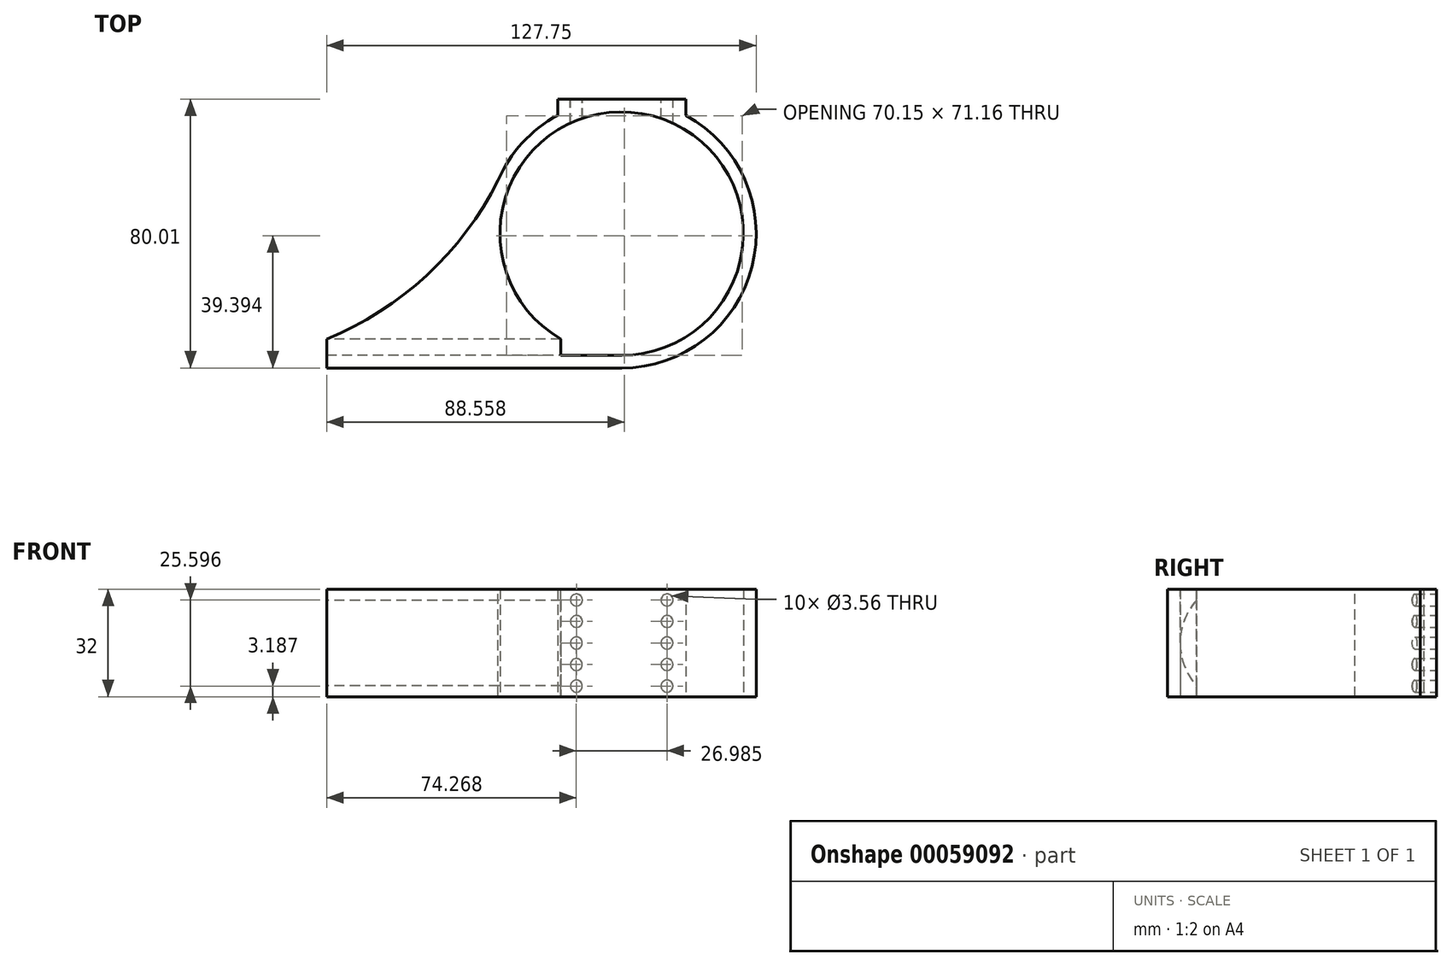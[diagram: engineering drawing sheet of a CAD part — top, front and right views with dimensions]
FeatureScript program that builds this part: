
annotation { "Feature Type Name" : "Feature", "Feature Type Description" : "" }
export const myFeature = defineFeature(function(context is Context, id is Id, definition is map)
    precondition{}
    {
        {
            var Q0;
            Q0=qCreatedBy(makeId("Top.planeOp"),FACE);
            var sketch = newSketch(context, id + "F0", { "sketchPlane" : qUnion([Q0])});
            skPoint(sketch, "E0.visualSharp", {"position": v(52.17, 65.91) * mm});
            skPoint(sketch, "E1.visualSharp", {"position": v(52.17, -14.1) * mm});
            skPoint(sketch, "E2.visualSharp", {"position": v(-27.84, 65.91) * mm});
            skLineSegment(sketch, "E3", {"start": v(12.16, 65.91) * mm, "end": v(12.16, 65.91) * mm});
            skArc(sketch, "E4.filletArc", {"start": v(-6.89, 61.09) * mm, "mid": v(-22.2, 46.38) * mm, "end": v(-27.84, 25.9) * mm});
            skLineSegment(sketch, "E5", {"start": v(52.17, 25.9) * mm, "end": v(52.17, 25.9) * mm});
            skArc(sketch, "E6.filletArc", {"start": v(52.17, 25.9) * mm, "mid": v(46.53, 46.38) * mm, "end": v(31.21, 61.09) * mm});
            skArc(sketch, "E7.filletArc", {"start": v(12.16, -14.1) * mm, "mid": v(40.45, -2.38) * mm, "end": v(52.17, 25.9) * mm});
            skLineSegment(sketch, "E8", {"start": v(12.16, -14.1) * mm, "end": v(-75.58, -14.1) * mm});
            skArc(sketch, "E9", {"start": v(12.16, -10.29) * mm, "mid": v(37.76, 0.31) * mm, "end": v(48.36, 25.9) * mm});
            skArc(sketch, "E10", {"start": v(48.36, 25.9) * mm, "mid": v(12.16, 62.1) * mm, "end": v(-24.03, 25.9) * mm});
            skLineSegment(sketch, "E11", {"start": v(-75.58, -14.1) * mm, "end": v(-75.58, -5.46) * mm});
            skArc(sketch, "E12", {"start": v(-24.03, 25.9) * mm, "mid": v(-19.17, 7.79) * mm, "end": v(-5.9, -5.46) * mm});
            skArc(sketch, "E13", {"start": v(-27.84, 25.9) * mm, "mid": v(-23.85, 8.48) * mm, "end": v(-12.66, -5.46) * mm});
            skLineSegment(sketch, "E14", {"start": v(12.16, -10.29) * mm, "end": v(-5.9, -10.29) * mm});
            skLineSegment(sketch, "E15", {"start": v(-5.9, -10.29) * mm, "end": v(-12.66, -10.29) * mm});
            skLineSegment(sketch, "E16", {"start": v(-5.9, -5.46) * mm, "end": v(-12.66, -5.46) * mm});
            skLineSegment(sketch, "E17", {"start": v(-5.9, -10.29) * mm, "end": v(-5.9, -5.46) * mm});
            skLineSegment(sketch, "E18", {"start": v(-5.9, -5.46) * mm, "end": v(-75.58, -5.46) * mm});
            skLineSegment(sketch, "E19", {"start": v(12.16, 65.91) * mm, "end": v(-6.89, 65.91) * mm});
            skLineSegment(sketch, "E20", {"start": v(12.16, 65.91) * mm, "end": v(31.21, 65.91) * mm});
            skLineSegment(sketch, "E21", {"start": v(-6.89, 65.91) * mm, "end": v(-6.89, 61.09) * mm});
            skLineSegment(sketch, "E22", {"start": v(31.21, 65.91) * mm, "end": v(31.21, 61.09) * mm});
            skSolve(sketch);
        }
        {
            var Q0;
            Q0=makeQuery(id+"F0.imprint","IMPRINT",FACE,{"disambiguationData":[TD([[makeQuery(id+"F0.imprint","IMPRINT",EDGE,{"derivedFrom":sQuery(id+"F0.wireOp",EDGE,"E4.filletArc")}),1.0]])]});
            extrude(context, id + "F1", {"entities" : qUnion([Q0]), "depth" : 32 * mm});
        }
        {
            var Q0;
            Q0=makeQuery(id+"F1.opExtrude","SWEPT_FACE",FACE,{"disambiguationData":[OSD([sQuery(id+"F0.wireOp",EDGE,"E11")])]});
            var sketch = newSketch(context, id + "F2", { "sketchPlane" : qUnion([Q0])});
            skLineSegment(sketch, "E23", {"start": v(5.46, 0) * mm, "end": v(5.46, 32) * mm});
            skArc(sketch, "E24", {"start": v(5.46, 3.3) * mm, "mid": v(10.29, 16) * mm, "end": v(5.46, 28.7) * mm});
            skLineSegment(sketch, "E25", {"start": v(5.46, 3.3) * mm, "end": v(5.46, 28.7) * mm});
            skSolve(sketch);
        }
        {
            var Q0;
            Q0=makeQuery(id+"F2.imprint","IMPRINT",FACE,{"disambiguationData":[TD([[makeQuery(id+"F2.imprint","IMPRINT",EDGE,{"derivedFrom":sQuery(id+"F2.wireOp",EDGE,"E24")}),1.0]])]});
            var Q1;
            Q1=sQuery(id+"F2.wireOp",EDGE,"E24");
            var Q2;
            Q2=sQuery(id+"F2.wireOp",EDGE,"E25");
            extrude(context, id + "F3", {"entities" : qUnion([Q0]), "operationType" : NewBodyOperationType.REMOVE, "surfaceEntities" : qUnion([Q1, Q2]), "oppositeDirection" : true, "depth" : 76.54 * mm});
        }
        {
            var Q0;
            Q0=makeQuery(id+"F1.opExtrude","SWEPT_FACE",FACE,{"disambiguationData":[OSD([sQuery(id+"F0.wireOp",EDGE,"E19"),sQuery(id+"F0.wireOp",EDGE,"E20")])]});
            var sketch = newSketch(context, id + "F4", { "sketchPlane" : qUnion([Q0])});
            skCircle(sketch, "E26", {"center": v(-25.64, 16) * mm, "radius": 1.78 * mm});
            skCircle(sketch, "E27", {"center": v(1.3, 16) * mm, "radius": 1.78 * mm});
            skCircle(sketch, "E28", {"center": v(-25.66, 28.78) * mm, "radius": 1.78 * mm});
            skCircle(sketch, "E29", {"center": v(1.3, 28.78) * mm, "radius": 1.78 * mm});
            skLineSegment(sketch, "E30", {"start": v(-12.16, 3.19) * mm, "end": v(-12.16, 3.23) * mm});
            skCircle(sketch, "E31", {"center": v(-25.64, 3.19) * mm, "radius": 1.78 * mm});
            skLineSegment(sketch, "E32", {"start": v(-12.16, 3.19) * mm, "end": v(-12.16, 3.19) * mm});
            skCircle(sketch, "E33", {"center": v(1.31, 3.19) * mm, "radius": 1.78 * mm});
            skLineSegment(sketch, "E34.trimOffspring", {"start": v(-12.16, 3.23) * mm, "end": v(-12.16, 3.19) * mm});
            skPoint(sketch, "E35.orphan", {"position": v(-12.16, 0) * mm});
            skPoint(sketch, "E36.start.orphan", {"position": v(-12.16, 32) * mm});
            skLineSegment(sketch, "E37", {"start": v(-12.16, 9.6) * mm, "end": v(-12.16, 9.6) * mm});
            skLineSegment(sketch, "E38", {"start": v(-12.17, 22.4) * mm, "end": v(-12.17, 22.4) * mm});
            skCircle(sketch, "E39", {"center": v(-25.67, 22.4) * mm, "radius": 1.78 * mm});
            skLineSegment(sketch, "E40", {"start": v(-25.65, 22.4) * mm, "end": v(-25.67, 22.4) * mm});
            skLineSegment(sketch, "E41", {"start": v(-12.2, 22.4) * mm, "end": v(-12.17, 22.4) * mm});
            skCircle(sketch, "E42", {"center": v(1.28, 22.4) * mm, "radius": 1.78 * mm});
            skCircle(sketch, "E43", {"center": v(-25.64, 9.6) * mm, "radius": 1.78 * mm});
            skCircle(sketch, "E44", {"center": v(1.31, 9.6) * mm, "radius": 1.78 * mm});
            skPoint(sketch, "E45.orphan", {"position": v(-12.18, 28.78) * mm});
            skPoint(sketch, "E46.orphan", {"position": v(-12.16, 16) * mm});
            skSolve(sketch);
        }
        {
            var Q0;
            Q0=makeQuery(id+"F4.imprint","IMPRINT",FACE,{"disambiguationData":[TD([[makeQuery(id+"F4.imprint","IMPRINT",EDGE,{"derivedFrom":sQuery(id+"F4.wireOp",EDGE,"E39")}),1.0]])]});
            var Q1;
            Q1=makeQuery(id+"F4.imprint","IMPRINT",FACE,{"disambiguationData":[TD([[makeQuery(id+"F4.imprint","IMPRINT",EDGE,{"derivedFrom":sQuery(id+"F4.wireOp",EDGE,"E28")}),1.0]])]});
            var Q2;
            Q2=makeQuery(id+"F4.imprint","IMPRINT",FACE,{"disambiguationData":[TD([[makeQuery(id+"F4.imprint","IMPRINT",EDGE,{"derivedFrom":sQuery(id+"F4.wireOp",EDGE,"E26")}),1.0]])]});
            var Q3;
            Q3=makeQuery(id+"F4.imprint","IMPRINT",FACE,{"disambiguationData":[TD([[makeQuery(id+"F4.imprint","IMPRINT",EDGE,{"derivedFrom":sQuery(id+"F4.wireOp",EDGE,"E43")}),1.0]])]});
            var Q4;
            Q4=makeQuery(id+"F4.imprint","IMPRINT",FACE,{"disambiguationData":[TD([[makeQuery(id+"F4.imprint","IMPRINT",EDGE,{"derivedFrom":sQuery(id+"F4.wireOp",EDGE,"E31")}),1.0]])]});
            var Q5;
            Q5=makeQuery(id+"F4.imprint","IMPRINT",FACE,{"disambiguationData":[TD([[makeQuery(id+"F4.imprint","IMPRINT",EDGE,{"derivedFrom":sQuery(id+"F4.wireOp",EDGE,"E33")}),1.0]])]});
            var Q6;
            Q6=makeQuery(id+"F4.imprint","IMPRINT",FACE,{"disambiguationData":[TD([[makeQuery(id+"F4.imprint","IMPRINT",EDGE,{"derivedFrom":sQuery(id+"F4.wireOp",EDGE,"E44")}),1.0]])]});
            var Q7;
            Q7=makeQuery(id+"F4.imprint","IMPRINT",FACE,{"disambiguationData":[TD([[makeQuery(id+"F4.imprint","IMPRINT",EDGE,{"derivedFrom":sQuery(id+"F4.wireOp",EDGE,"E27")}),1.0]])]});
            var Q8;
            Q8=makeQuery(id+"F4.imprint","IMPRINT",FACE,{"disambiguationData":[TD([[makeQuery(id+"F4.imprint","IMPRINT",EDGE,{"derivedFrom":sQuery(id+"F4.wireOp",EDGE,"E42")}),1.0]])]});
            var Q9;
            Q9=makeQuery(id+"F4.imprint","IMPRINT",FACE,{"disambiguationData":[TD([[makeQuery(id+"F4.imprint","IMPRINT",EDGE,{"derivedFrom":sQuery(id+"F4.wireOp",EDGE,"E29")}),1.0]])]});
            var Q10;
            Q10=sQuery(id+"F4.wireOp",EDGE,"E28");
            extrude(context, id + "F5", {"entities" : qUnion([Q0, Q1, Q2, Q3, Q4, Q5, Q6, Q7, Q8, Q9]), "operationType" : NewBodyOperationType.REMOVE, "surfaceEntities" : qUnion([Q10]), "oppositeDirection" : true, "depth" : 44.6 * mm});
        }
        {
            var Q0;
            Q0=makeQuery(id+"F1.opExtrude","CAP_FACE",FACE,{"disambiguationData":[OSD([sQuery(id+"F0.wireOp",EDGE,"E4.filletArc"),sQuery(id+"F0.wireOp",EDGE,"E6.filletArc"),sQuery(id+"F0.wireOp",EDGE,"E7.filletArc"),sQuery(id+"F0.wireOp",EDGE,"E8"),sQuery(id+"F0.wireOp",EDGE,"E9"),sQuery(id+"F0.wireOp",EDGE,"E10"),sQuery(id+"F0.wireOp",EDGE,"E11"),sQuery(id+"F0.wireOp",EDGE,"E12"),sQuery(id+"F0.wireOp",EDGE,"E13"),sQuery(id+"F0.wireOp",EDGE,"E14"),sQuery(id+"F0.wireOp",EDGE,"E15"),sQuery(id+"F0.wireOp",EDGE,"E16"),sQuery(id+"F0.wireOp",EDGE,"E17"),sQuery(id+"F0.wireOp",EDGE,"E18"),sQuery(id+"F0.wireOp",EDGE,"E19"),sQuery(id+"F0.wireOp",EDGE,"E20"),sQuery(id+"F0.wireOp",EDGE,"E21"),sQuery(id+"F0.wireOp",EDGE,"E22")])],"isStart":false});
            var sketch = newSketch(context, id + "F6", { "sketchPlane" : qUnion([Q0])});
            skArc(sketch, "E47", {"start": v(-75.58, -5.46) * mm, "mid": v(-45.78, 13.49) * mm, "end": v(-24.58, 41.72) * mm});
            skArc(sketch, "E48", {"start": v(-24.58, 41.72) * mm, "mid": v(-23.91, 16.8) * mm, "end": v(-12.66, -5.46) * mm});
            skLineSegment(sketch, "E49", {"start": v(-75.58, -5.46) * mm, "end": v(-12.66, -5.46) * mm});
            skSolve(sketch);
        }
        {
            var Q0;
            Q0 = qSketchRegion(id + "F6", true);
            extrude(context, id + "F7", {"entities" : qUnion([Q0]), "operationType" : NewBodyOperationType.ADD, "oppositeDirection" : true, "depth" : 32 * mm});
        }
    });
